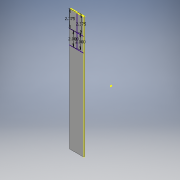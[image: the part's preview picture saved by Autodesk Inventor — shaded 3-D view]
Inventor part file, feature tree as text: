
AUTODESK INVENTOR PART (.ipt)
format: ipt  version: 2017 (Build 210142000, 142)  size: 109,056 bytes
history: native  units: in
note: dims shown in document units (in); Inventor stores cm internally (conversion verified against a paired STEP export)
features: sketch x4, extrude x1
ambient origin geometry x8: Origin, YZ Plane, XZ Plane, XY Plane, X Axis, Y Axis, Z Axis, Center Point
bodies: Solid1 (feature_tree)
feature tree (5):
  extrude  "Extrusion1"  Depth=16.875in
  sketch  "Sketch2"  dims[d2=0.125in d3=0.0in]
  sketch  "Sketch3"  dims[d4=2.375in]
  sketch  "Sketch4"  dims[d5=2.375in d6=2.375in d7=2.0in d8=2.0in]
  sketch  "Sketch1"  dims[d0=2.0in d1=16.875in]
